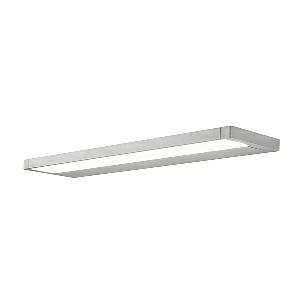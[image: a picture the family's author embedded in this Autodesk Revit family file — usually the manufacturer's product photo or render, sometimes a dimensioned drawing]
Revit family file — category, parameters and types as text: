
# Revit family: zera_bath_-_zew_3000_830_00812053_def6
name_source: partatom
category: Lighting Fixtures
units: mm (PartAtom-declared; Revit-internal decimal feet)

## family parameters
Cut with Voids When Loaded = No
Host = Face
Light Source = No
Part Type = Normal
Room Calculation Point = No
Round Connector Dimension = Use Diameter
Shared = No

## types (1)
- ZERA.bath - ZEW 3000/830 (1 x LED, 3300 lm, 3000K)
    Apparent Load = 27 VA
    Approval mark = CE
    CIE Flux Codes = 47 78 95 39 100
    Color Rendering = 80-89
    Color Temperature = 3000K
    Control Gear = Electronic ballast
    Default Elevation = 2000 mm  [stored 6.56168 ft]
    Description = ZEW 3000/830|Wall-mounted luminaire|light source:   Warm white   |work equipment: Power supply unit|luminous flux: 3300 lm|light distribution: Direct/indirect|class of protection: I|technology: Switchable|mains lead: Connector 2 pin|glare control: Diffusor|special features: DIN EN 60598-2-25|
    Frequency = 50 Hz, 60 Hz
    Height = 29 mm
    Lamp = 1 x LED
    Lamp Light Flux = 3300 lm
    Lamp count = 1
    Length = 600 mm
    Luminous efficacy = 122 lm/W
    Manufacturer = Waldmann
    ModVariant = No
    Model = 00812053
    Mounting Place = Wall
    Mounting Type = Surface mounted
    Number of Poles = 1
    OnlyDefault = Yes
    Power Factor = 1
    Product Name = ZERA.bath - ZEW 3000/830
    Product group = Wall mounted Luminaire
    ProductGroupID = 20
    Protection Class = Protection class I
    Protection Degree = IP 44
    RLX_Detail_Level = 1
    RLX_Emergency_Light_Flux = 0 lm
    RLX_Emergency_Type = 0
    RLX_Emergency_Type_DB = No
    RlxData = <blob elided: 35253 chars, md5=10bc63ef>
    Socket = socket
    Standby Power = 0 W
    System Light Flux = 3300 lm
    System Power = 27 W
    Type Comments = Product without accessories
    Type Image = zera_bath_20_w.jpg
    URL = http://relux.com
    VarID = ---
    Voltage = 230 V
    Voltage Range = 220-240 V
    Weight = 0.00 kg
    Width = 142 mm

note: [stored X ft] marks values corroborated as IEEE doubles in the binary element streams (Revit-internal decimal feet)

## geometry (parser evidence)
native form markers: Blend x4, Sweep x13
no freeform markers — native parametric forms only
